# Revit family: Haworth_Hobo_Sofas_OneArm
name_source: partatom
category: Furniture
revit_build: Autodesk Revit 2018 (Build: 20170223_1515(x64)
units: mm (PartAtom-declared; Revit-internal decimal feet)

## family parameters
Always vertical = Yes
Cut with Voids When Loaded = No
OmniClass Number = 23.40.70.14.64.21
OmniClass Title = Systems Furniture
Room Calculation Point = No
Shared = No
Work Plane-Based = No

## types (1)
- HCCE-HBL2 - Two Seats Sofa with One Arm
    Actual Depth = 33 1/2"
    Actual Height = 28 3/4"
    Actual Width = 69"
    Arm Offset = 7 1/4"
    Assembly Code = E2020200
    Cushion Offset = 6"
    Description = Haworth Hobo Two Seats Sofa with One Arm
    Leg Offset = 4 235/256"
    Manufacturer = Haworth
    Model = HCCE-HBL
    Revision Number = 1
    Seat Width = 63"
    Size = Verify Final Dim. w/ Haworth
    URL = http://www.haworth.com
    URL - Product = https://www.haworth.com
    Warranty = http://www.haworth.com

## geometry (parser evidence)
native form markers: Extrusion x1, Sweep x5
no freeform markers — native parametric forms only
